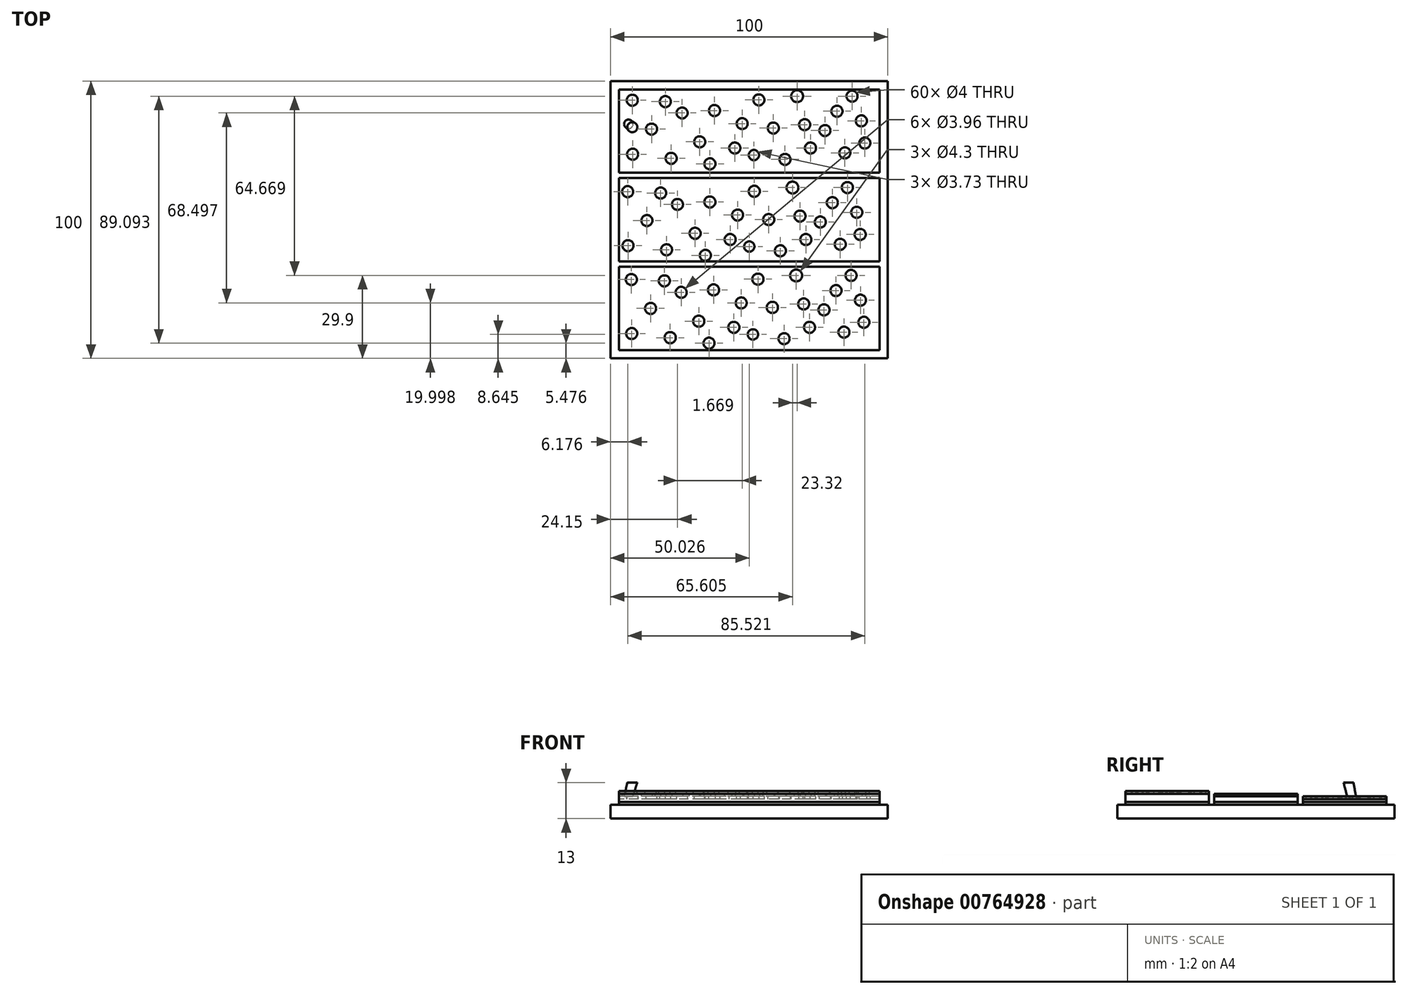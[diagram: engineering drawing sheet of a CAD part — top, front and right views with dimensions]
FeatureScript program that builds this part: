
annotation { "Feature Type Name" : "Feature", "Feature Type Description" : "" }
export const myFeature = defineFeature(function(context is Context, id is Id, definition is map)
    precondition{}
    {
        {
            var Q0;
            Q0=qCreatedBy(makeId("Top.planeOp"),FACE);
            var sketch = newSketch(context, id + "F0", { "sketchPlane" : qUnion([Q0])});
            skLineSegment(sketch, "E0.bottom", {"start": v(50, -50) * mm, "end": v(-50, -50) * mm});
            skLineSegment(sketch, "E0.top", {"start": v(50, 50) * mm, "end": v(-50, 50) * mm});
            skLineSegment(sketch, "E0.left", {"start": v(50, -50) * mm, "end": v(50, 50) * mm});
            skLineSegment(sketch, "E0.right", {"start": v(-50, -50) * mm, "end": v(-50, 50) * mm});
            skPoint(sketch, "E0.middle", {"position": v(0, 0) * mm});
            skSolve(sketch);
        }
        {
            var Q0;
            Q0=makeQuery(id+"F0.imprint","IMPRINT",FACE,{"disambiguationData":[TD([[makeQuery(id+"F0.imprint","IMPRINT",EDGE,{"derivedFrom":sQuery(id+"F0.wireOp",EDGE,"E0.bottom")}),-1.0]])]});
            extrude(context, id + "F1", {"entities" : qUnion([Q0]), "depth" : 5 * mm, "offsetDistance" : 25 * mm});
        }
        {
            var Q0;
            Q0=makeQuery(id+"F1.opExtrude","CAP_FACE",FACE,{"disambiguationData":[OSD([sQuery(id+"F0.wireOp",EDGE,"E0.bottom"),sQuery(id+"F0.wireOp",EDGE,"E0.top"),sQuery(id+"F0.wireOp",EDGE,"E0.left"),sQuery(id+"F0.wireOp",EDGE,"E0.right")])],"isStart":false});
            var sketch = newSketch(context, id + "F2", { "sketchPlane" : qUnion([Q0])});
            skLineSegment(sketch, "E1.bottom", {"start": v(47, -15) * mm, "end": v(-47, -15) * mm});
            skLineSegment(sketch, "E1.top", {"start": v(47, 15) * mm, "end": v(-47, 15) * mm});
            skLineSegment(sketch, "E1.left", {"start": v(47, -15) * mm, "end": v(47, 15) * mm});
            skLineSegment(sketch, "E1.right", {"start": v(-47, -15) * mm, "end": v(-47, 15) * mm});
            skPoint(sketch, "E1.middle", {"position": v(0, 0) * mm});
            skLineSegment(sketch, "E2.bottom", {"start": v(47, 17) * mm, "end": v(-47, 17) * mm});
            skLineSegment(sketch, "E2.top", {"start": v(47, 47) * mm, "end": v(-47, 47) * mm});
            skLineSegment(sketch, "E2.left", {"start": v(47, 17) * mm, "end": v(47, 47) * mm});
            skLineSegment(sketch, "E2.right", {"start": v(-47, 17) * mm, "end": v(-47, 47) * mm});
            skPoint(sketch, "E2.middle", {"position": v(0, 32) * mm});
            skLineSegment(sketch, "E3.bottom", {"start": v(47, -47) * mm, "end": v(-47, -47) * mm});
            skLineSegment(sketch, "E3.top", {"start": v(47, -17) * mm, "end": v(-47, -17) * mm});
            skLineSegment(sketch, "E3.left", {"start": v(47, -47) * mm, "end": v(47, -17) * mm});
            skLineSegment(sketch, "E3.right", {"start": v(-47, -47) * mm, "end": v(-47, -17) * mm});
            skPoint(sketch, "E3.middle", {"position": v(0, -32) * mm});
            skSolve(sketch);
        }
        {
            var Q0;
            Q0=makeQuery(id+"F2.imprint","IMPRINT",FACE,{"disambiguationData":[TD([[makeQuery(id+"F2.imprint","IMPRINT",EDGE,{"derivedFrom":sQuery(id+"F2.wireOp",EDGE,"E2.bottom")}),-1.0]])]});
            var Q1;
            Q1=makeQuery(id+"F2.imprint","IMPRINT",FACE,{"disambiguationData":[TD([[makeQuery(id+"F2.imprint","IMPRINT",EDGE,{"derivedFrom":sQuery(id+"F2.wireOp",EDGE,"E1.bottom")}),-1.0]])]});
            var Q2;
            Q2=makeQuery(id+"F2.imprint","IMPRINT",FACE,{"disambiguationData":[TD([[makeQuery(id+"F2.imprint","IMPRINT",EDGE,{"derivedFrom":sQuery(id+"F2.wireOp",EDGE,"E3.bottom")}),-1.0]])]});
            extrude(context, id + "F3", {"entities" : qUnion([Q0, Q1, Q2]), "depth" : 1 * mm, "offsetDistance" : 25 * mm});
        }
        {
            var Q0;
            Q0=makeQuery(id+"F3.opExtrude","CAP_FACE",FACE,{"disambiguationData":[OSD([sQuery(id+"F2.wireOp",EDGE,"E2.bottom"),sQuery(id+"F2.wireOp",EDGE,"E2.top"),sQuery(id+"F2.wireOp",EDGE,"E2.left"),sQuery(id+"F2.wireOp",EDGE,"E2.right")])],"isStart":false});
            extrude(context, id + "F4", {"entities" : qUnion([Q0]), "depth" : 1 * mm, "offsetDistance" : 25 * mm});
        }
        {
            var Q0;
            Q0=makeQuery(id+"F3.opExtrude","CAP_FACE",FACE,{"disambiguationData":[OSD([sQuery(id+"F2.wireOp",EDGE,"E1.bottom"),sQuery(id+"F2.wireOp",EDGE,"E1.top"),sQuery(id+"F2.wireOp",EDGE,"E1.left"),sQuery(id+"F2.wireOp",EDGE,"E1.right")])],"isStart":false});
            extrude(context, id + "F5", {"entities" : qUnion([Q0]), "depth" : 2 * mm, "offsetDistance" : 25 * mm});
        }
        {
            var Q0;
            Q0=makeQuery(id+"F3.opExtrude","CAP_FACE",FACE,{"disambiguationData":[OSD([sQuery(id+"F2.wireOp",EDGE,"E3.bottom"),sQuery(id+"F2.wireOp",EDGE,"E3.top"),sQuery(id+"F2.wireOp",EDGE,"E3.left"),sQuery(id+"F2.wireOp",EDGE,"E3.right")])],"isStart":false});
            extrude(context, id + "F6", {"entities" : qUnion([Q0]), "depth" : 3 * mm, "offsetDistance" : 25 * mm});
        }
        {
            var Q0;
            Q0=makeQuery(id+"F6.opExtrude","CAP_FACE",FACE,{"disambiguationData":[OSD([sQuery(id+"F2.wireOp",EDGE,"E3.bottom"),sQuery(id+"F2.wireOp",EDGE,"E3.top"),sQuery(id+"F2.wireOp",EDGE,"E3.left"),sQuery(id+"F2.wireOp",EDGE,"E3.right")])],"isStart":false});
            var Q1;
            Q1=makeQuery(id+"F5.opExtrude","CAP_FACE",FACE,{"disambiguationData":[OSD([sQuery(id+"F2.wireOp",EDGE,"E1.bottom"),sQuery(id+"F2.wireOp",EDGE,"E1.top"),sQuery(id+"F2.wireOp",EDGE,"E1.left"),sQuery(id+"F2.wireOp",EDGE,"E1.right")])],"isStart":false});
            var Q2;
            Q2=makeQuery(id+"F4.opExtrude","CAP_FACE",FACE,{"disambiguationData":[OSD([sQuery(id+"F2.wireOp",EDGE,"E2.bottom"),sQuery(id+"F2.wireOp",EDGE,"E2.top"),sQuery(id+"F2.wireOp",EDGE,"E2.left"),sQuery(id+"F2.wireOp",EDGE,"E2.right")])],"isStart":false});
            extrude(context, id + "F7", {"entities" : qUnion([Q0, Q1, Q2]), "depth" : 1 * mm, "offsetDistance" : 25 * mm});
        }
        {
            var Q0;
            Q0=makeQuery(id+"F7.opExtrude","CAP_FACE",FACE,{"disambiguationData":[OSD([sQuery(id+"F2.wireOp",EDGE,"E3.bottom"),sQuery(id+"F2.wireOp",EDGE,"E3.top"),sQuery(id+"F2.wireOp",EDGE,"E3.left"),sQuery(id+"F2.wireOp",EDGE,"E3.right")])],"isStart":false});
            var sketch = newSketch(context, id + "F8", { "sketchPlane" : qUnion([Q0])});
            skCircle(sketch, "E4", {"center": v(-35.55, -32) * mm, "radius": 2 * mm});
            skCircle(sketch, "E5", {"center": v(-18.19, -36.58) * mm, "radius": 2 * mm});
            skCircle(sketch, "E6", {"center": v(-12.85, -25.3) * mm, "radius": 2 * mm});
            skCircle(sketch, "E7", {"center": v(8.36, -31.62) * mm, "radius": 2 * mm});
            skCircle(sketch, "E8", {"center": v(19.64, -30.38) * mm, "radius": 2 * mm});
            skCircle(sketch, "E9", {"center": v(31.3, -25.54) * mm, "radius": 2 * mm});
            skCircle(sketch, "E10", {"center": v(34.16, -40.55) * mm, "radius": 2 * mm});
            skCircle(sketch, "E11", {"center": v(12.57, -42.9) * mm, "radius": 2 * mm});
            skCircle(sketch, "E12", {"center": v(3.15, -21.45) * mm, "radius": 2 * mm});
            skCircle(sketch, "E13", {"center": v(-5.53, -38.81) * mm, "radius": 2 * mm});
            skCircle(sketch, "E14", {"center": v(-30.59, -22.07) * mm, "radius": 2 * mm});
            skCircle(sketch, "E15", {"center": v(-42.37, -41.05) * mm, "radius": 2 * mm});
            skCircle(sketch, "E16", {"center": v(40.11, -29.01) * mm, "radius": 2 * mm});
            skCircle(sketch, "E17", {"center": v(-28.48, -42.53) * mm, "radius": 2 * mm});
            skCircle(sketch, "E18", {"center": v(21.75, -38.81) * mm, "radius": 2 * mm});
            skCircle(sketch, "E19", {"center": v(-42.5, -21.57) * mm, "radius": 2 * mm});
            skCircle(sketch, "E20", {"center": v(-2.87, -30) * mm, "radius": 1.98 * mm});
            skCircle(sketch, "E21", {"center": v(16.93, -20.1) * mm, "radius": 2.15 * mm});
            skCircle(sketch, "E22", {"center": v(-24.52, -26.17) * mm, "radius": 1.98 * mm});
            skCircle(sketch, "E23", {"center": v(36.73, -20.1) * mm, "radius": 2 * mm});
            skCircle(sketch, "E24", {"center": v(41.36, -37) * mm, "radius": 2 * mm});
            skCircle(sketch, "E25", {"center": v(26.97, -32.5) * mm, "radius": 2 * mm});
            skCircle(sketch, "E26", {"center": v(1.35, -41.36) * mm, "radius": 1.87 * mm});
            skCircle(sketch, "E27", {"center": v(-14.49, -44.52) * mm, "radius": 2 * mm});
            skSolve(sketch);
        }
        {
            var Q0;
            Q0=qSketchRegion(id+"F8",true);
            extrude(context, id + "F9", {"entities" : qUnion([Q0]), "operationType" : NewBodyOperationType.REMOVE, "oppositeDirection" : true, "depth" : 1 * mm, "offsetDistance" : 25 * mm});
        }
        {
            var Q0;
            Q0=makeQuery(id+"F7.opExtrude","CAP_FACE",FACE,{"disambiguationData":[OSD([sQuery(id+"F2.wireOp",EDGE,"E1.bottom"),sQuery(id+"F2.wireOp",EDGE,"E1.top"),sQuery(id+"F2.wireOp",EDGE,"E1.left"),sQuery(id+"F2.wireOp",EDGE,"E1.right")])],"isStart":false});
            var sketch = newSketch(context, id + "F10", { "sketchPlane" : qUnion([Q0])});
            skCircle(sketch, "E28", {"center": v(-36.88, -0.3) * mm, "radius": 2 * mm});
            skCircle(sketch, "E29", {"center": v(-19.51, -4.9) * mm, "radius": 2 * mm});
            skCircle(sketch, "E30", {"center": v(-14.18, 6.4) * mm, "radius": 2 * mm});
            skCircle(sketch, "E31", {"center": v(7.03, 0.07) * mm, "radius": 2 * mm});
            skCircle(sketch, "E32", {"center": v(18.32, 1.3) * mm, "radius": 2 * mm});
            skCircle(sketch, "E33", {"center": v(29.98, 6.15) * mm, "radius": 2 * mm});
            skCircle(sketch, "E34", {"center": v(32.83, -8.86) * mm, "radius": 2 * mm});
            skCircle(sketch, "E35", {"center": v(11.25, -11.22) * mm, "radius": 2 * mm});
            skCircle(sketch, "E36", {"center": v(1.82, 10.24) * mm, "radius": 2 * mm});
            skCircle(sketch, "E37", {"center": v(-6.86, -7.13) * mm, "radius": 2 * mm});
            skCircle(sketch, "E38", {"center": v(-31.92, 9.62) * mm, "radius": 2 * mm});
            skCircle(sketch, "E39", {"center": v(-43.7, -9.36) * mm, "radius": 2 * mm});
            skCircle(sketch, "E40", {"center": v(38.78, 2.67) * mm, "radius": 2 * mm});
            skCircle(sketch, "E41", {"center": v(-29.8, -10.85) * mm, "radius": 2 * mm});
            skCircle(sketch, "E42", {"center": v(20.43, -7.13) * mm, "radius": 2 * mm});
            skCircle(sketch, "E43", {"center": v(-43.82, 10.12) * mm, "radius": 2 * mm});
            skCircle(sketch, "E44", {"center": v(-4.2, 1.69) * mm, "radius": 1.98 * mm});
            skCircle(sketch, "E45", {"center": v(15.6, 11.59) * mm, "radius": 2.15 * mm});
            skCircle(sketch, "E46", {"center": v(-25.85, 5.52) * mm, "radius": 1.98 * mm});
            skCircle(sketch, "E47", {"center": v(35.4, 11.59) * mm, "radius": 2 * mm});
            skCircle(sketch, "E48", {"center": v(40.03, -5.31) * mm, "radius": 2 * mm});
            skCircle(sketch, "E49", {"center": v(25.64, -0.82) * mm, "radius": 2 * mm});
            skCircle(sketch, "E50", {"center": v(0.03, -9.67) * mm, "radius": 1.87 * mm});
            skCircle(sketch, "E51", {"center": v(-15.82, -12.84) * mm, "radius": 2 * mm});
            skSolve(sketch);
        }
        {
            var Q0;
            Q0=qSketchRegion(id+"F10",true);
            extrude(context, id + "F11", {"entities" : qUnion([Q0]), "operationType" : NewBodyOperationType.REMOVE, "oppositeDirection" : true, "depth" : 1 * mm, "offsetDistance" : 25 * mm});
        }
        {
            var Q0;
            Q0=makeQuery(id+"F7.opExtrude","CAP_FACE",FACE,{"disambiguationData":[OSD([sQuery(id+"F2.wireOp",EDGE,"E2.bottom"),sQuery(id+"F2.wireOp",EDGE,"E2.top"),sQuery(id+"F2.wireOp",EDGE,"E2.left"),sQuery(id+"F2.wireOp",EDGE,"E2.right")])],"isStart":false});
            var sketch = newSketch(context, id + "F12", { "sketchPlane" : qUnion([Q0])});
            skCircle(sketch, "E52", {"center": v(-35.2, 32.68) * mm, "radius": 2 * mm});
            skCircle(sketch, "E53", {"center": v(-17.84, 28.09) * mm, "radius": 2 * mm});
            skCircle(sketch, "E54", {"center": v(-12.51, 39.38) * mm, "radius": 2 * mm});
            skCircle(sketch, "E55", {"center": v(8.7, 33.05) * mm, "radius": 2 * mm});
            skCircle(sketch, "E56", {"center": v(19.99, 34.29) * mm, "radius": 2 * mm});
            skCircle(sketch, "E57", {"center": v(31.65, 39.13) * mm, "radius": 2 * mm});
            skCircle(sketch, "E58", {"center": v(34.5, 24.12) * mm, "radius": 2 * mm});
            skCircle(sketch, "E59", {"center": v(12.92, 21.76) * mm, "radius": 2 * mm});
            skCircle(sketch, "E60", {"center": v(3.49, 43.22) * mm, "radius": 2 * mm});
            skCircle(sketch, "E61", {"center": v(-5.2, 25.86) * mm, "radius": 2 * mm});
            skCircle(sketch, "E62", {"center": v(-30.25, 42.6) * mm, "radius": 2 * mm});
            skCircle(sketch, "E63", {"center": v(-42.03, 23.62) * mm, "radius": 2 * mm});
            skCircle(sketch, "E64", {"center": v(40.45, 35.65) * mm, "radius": 2 * mm});
            skCircle(sketch, "E65", {"center": v(-28.14, 22.13) * mm, "radius": 2 * mm});
            skCircle(sketch, "E66", {"center": v(22.1, 25.86) * mm, "radius": 2 * mm});
            skCircle(sketch, "E67", {"center": v(-42.16, 43.1) * mm, "radius": 2 * mm});
            skCircle(sketch, "E68", {"center": v(-2.53, 34.67) * mm, "radius": 1.98 * mm});
            skCircle(sketch, "E69", {"center": v(17.27, 44.57) * mm, "radius": 2.15 * mm});
            skCircle(sketch, "E70", {"center": v(-24.18, 38.5) * mm, "radius": 1.98 * mm});
            skCircle(sketch, "E71", {"center": v(37.08, 44.57) * mm, "radius": 2 * mm});
            skCircle(sketch, "E72", {"center": v(41.7, 27.67) * mm, "radius": 2 * mm});
            skCircle(sketch, "E73", {"center": v(27.3, 32.16) * mm, "radius": 2 * mm});
            skCircle(sketch, "E74", {"center": v(1.7, 23.31) * mm, "radius": 1.87 * mm});
            skCircle(sketch, "E75", {"center": v(-14.15, 20.14) * mm, "radius": 2 * mm});
            skSolve(sketch);
        }
        {
            var Q0;
            Q0=qSketchRegion(id+"F12",true);
            extrude(context, id + "F13", {"entities" : qUnion([Q0]), "operationType" : NewBodyOperationType.REMOVE, "oppositeDirection" : true, "depth" : 1 * mm, "offsetDistance" : 25 * mm});
        }
        {
            var Q0;
            Q0=makeQuery(id+"F7.opExtrude","CAP_FACE",FACE,{"disambiguationData":[OSD([sQuery(id+"F2.wireOp",EDGE,"E2.bottom"),sQuery(id+"F2.wireOp",EDGE,"E2.top"),sQuery(id+"F2.wireOp",EDGE,"E2.left"),sQuery(id+"F2.wireOp",EDGE,"E2.right")])],"isStart":false});
            var sketch = newSketch(context, id + "F14", { "sketchPlane" : qUnion([Q0])});
            skCircle(sketch, "E76", {"center": v(-43.5, 34.5) * mm, "radius": 1.62 * mm});
            skSolve(sketch);
        }
        {
            var Q0;
            Q0=makeQuery(id+"F14.imprint","IMPRINT",FACE,{"disambiguationData":[TD([[makeQuery(id+"F14.imprint","IMPRINT",EDGE,{"derivedFrom":sQuery(id+"F14.wireOp",EDGE,"E76")}),-1.0]])]});
            cPlane(context, id + "F15", {"entities" : qUnion([Q0]), "cplaneType" : CPlaneType.OFFSET, "offset" : 5 * mm, "width" : 150 * mm, "height" : 150 * mm});
        }
        {
            var Q0;
            Q0=qCreatedBy(id+"F15.planeOp",FACE);
            var sketch = newSketch(context, id + "F16", { "sketchPlane" : qUnion([Q0])});
            skCircle(sketch, "E77", {"center": v(-42.15, 33.38) * mm, "radius": 1.8 * mm});
            skSolve(sketch);
        }
        {
            var Q1;
            Q1=makeQuery(id+"F16.imprint","IMPRINT",FACE,{"disambiguationData":[TD([[makeQuery(id+"F16.imprint","IMPRINT",EDGE,{"derivedFrom":sQuery(id+"F16.wireOp",EDGE,"E77")}),1.0]])]});
            var Q2;
            Q2=makeQuery(id+"F14.imprint","IMPRINT",FACE,{"disambiguationData":[TD([[makeQuery(id+"F14.imprint","IMPRINT",EDGE,{"derivedFrom":sQuery(id+"F14.wireOp",EDGE,"E76")}),1.0]])]});
            loft(context, id + "F17", {"sheetProfilesArray" : [{ "sheetProfileEntities" : qUnion([Q1]) }, { "sheetProfileEntities" : qUnion([Q2]) }]});
        }
    });
